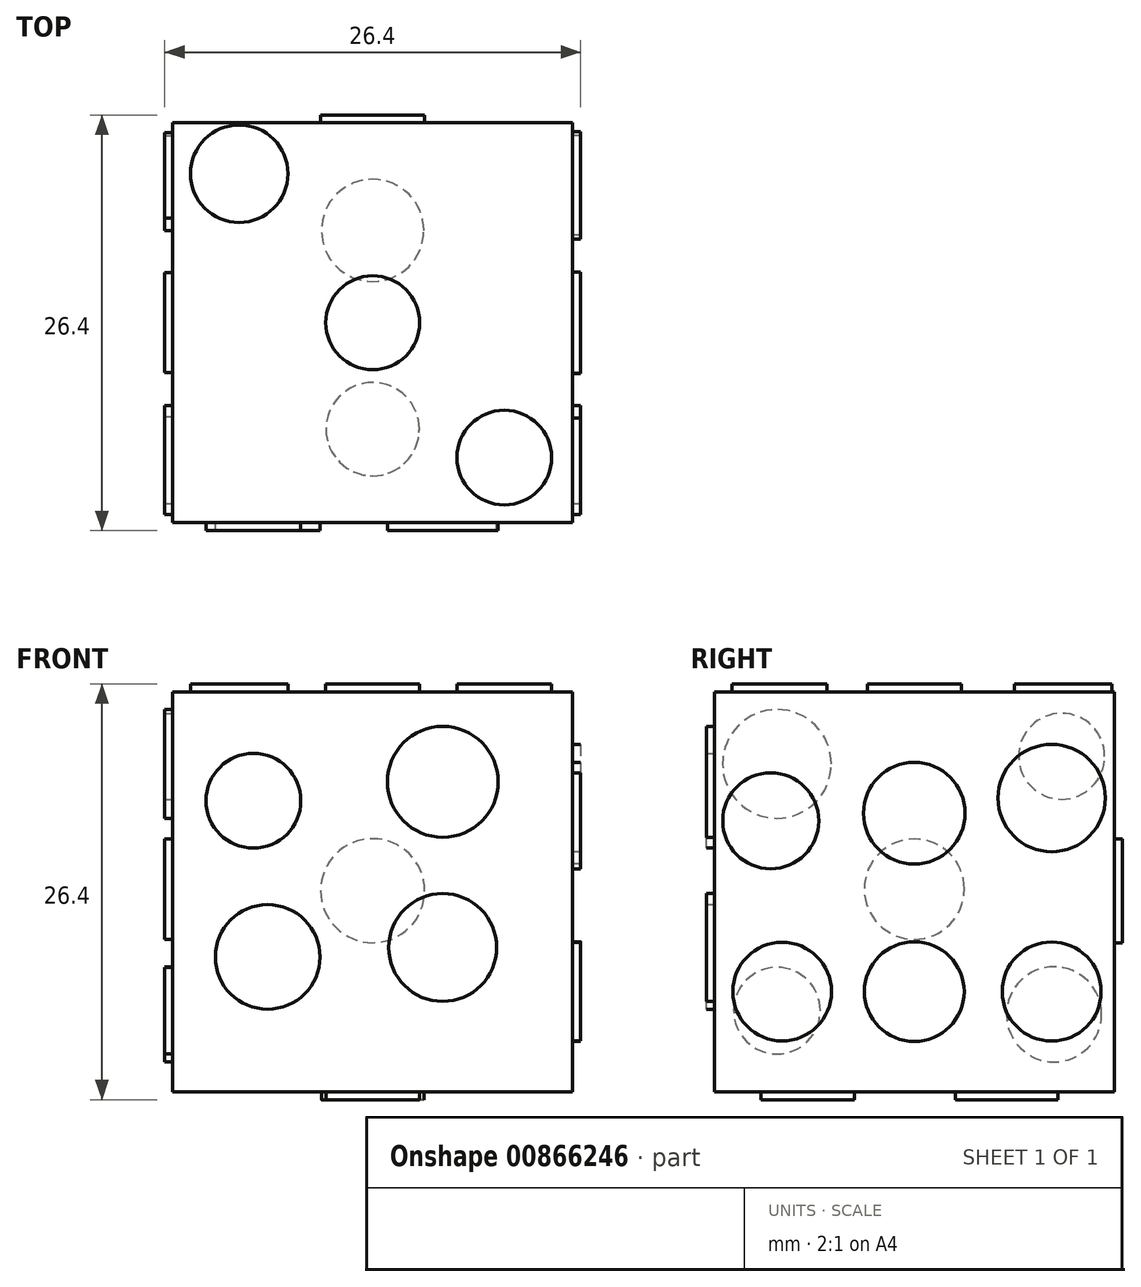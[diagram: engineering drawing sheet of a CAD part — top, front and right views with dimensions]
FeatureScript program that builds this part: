
annotation { "Feature Type Name" : "Feature", "Feature Type Description" : "" }
export const myFeature = defineFeature(function(context is Context, id is Id, definition is map)
    precondition{}
    {
        {
            var Q0;
            Q0=qCreatedBy(makeId("Top.planeOp"),FACE);
            var sketch = newSketch(context, id + "F0", { "sketchPlane" : qUnion([Q0])});
            skLineSegment(sketch, "E0.bottom", {"start": v(12.7, -12.7) * mm, "end": v(-12.7, -12.7) * mm});
            skLineSegment(sketch, "E0.top", {"start": v(12.7, 12.7) * mm, "end": v(-12.7, 12.7) * mm});
            skLineSegment(sketch, "E0.left", {"start": v(12.7, -12.7) * mm, "end": v(12.7, 12.7) * mm});
            skLineSegment(sketch, "E0.right", {"start": v(-12.7, -12.7) * mm, "end": v(-12.7, 12.7) * mm});
            skPoint(sketch, "E0.middle", {"position": v(0, 0) * mm});
            skSolve(sketch);
        }
        {
            var Q0;
            Q0 = qSketchRegion(id + "F0", true);
            extrude(context, id + "F1", {"entities" : qUnion([Q0]), "depth" : 25.4 * mm, "offsetDistance" : 25 * mm});
        }
        {
            var Q0;
            Q0=makeQuery(id+"F1.opExtrude","SWEPT_FACE",FACE,{"disambiguationData":[OSD([sQuery(id+"F0.wireOp",EDGE,"E0.top")])]});
            var sketch = newSketch(context, id + "F2", { "sketchPlane" : qUnion([Q0])});
            skCircle(sketch, "E1", {"center": v(0, 12.77) * mm, "radius": 3.3 * mm});
            skSolve(sketch);
        }
        {
            var Q0;
            Q0 = qSketchRegion(id + "F2", true);
            extrude(context, id + "F3", {"entities" : qUnion([Q0]), "operationType" : NewBodyOperationType.ADD, "depth" : .5 * mm, "offsetDistance" : 25 * mm});
        }
        {
            var Q0;
            Q0=makeQuery(id+"F1.opExtrude","CAP_FACE",FACE,{"disambiguationData":[OSD([sQuery(id+"F0.wireOp",EDGE,"E0.bottom"),sQuery(id+"F0.wireOp",EDGE,"E0.top"),sQuery(id+"F0.wireOp",EDGE,"E0.left"),sQuery(id+"F0.wireOp",EDGE,"E0.right")])],"isStart":true});
            var sketch = newSketch(context, id + "F4", { "sketchPlane" : qUnion([Q0])});
            skCircle(sketch, "E2", {"center": v(0, -5.86) * mm, "radius": 3.25 * mm});
            skCircle(sketch, "E3", {"center": v(0, 6.76) * mm, "radius": 2.96 * mm});
            skSolve(sketch);
        }
        {
            var Q0;
            Q0 = qSketchRegion(id + "F4", true);
            extrude(context, id + "F5", {"entities" : qUnion([Q0]), "operationType" : NewBodyOperationType.ADD, "depth" : .5 * mm, "offsetDistance" : 25 * mm});
        }
        {
            var Q0;
            Q0=makeQuery(id+"F1.opExtrude","CAP_FACE",FACE,{"disambiguationData":[OSD([sQuery(id+"F0.wireOp",EDGE,"E0.bottom"),sQuery(id+"F0.wireOp",EDGE,"E0.top"),sQuery(id+"F0.wireOp",EDGE,"E0.left"),sQuery(id+"F0.wireOp",EDGE,"E0.right")])],"isStart":false});
            var sketch = newSketch(context, id + "F6", { "sketchPlane" : qUnion([Q0])});
            skCircle(sketch, "E4", {"center": v(8.36, -8.57) * mm, "radius": 3 * mm});
            skCircle(sketch, "E5", {"center": v(0, 0) * mm, "radius": 2.98 * mm});
            skCircle(sketch, "E6", {"center": v(-8.48, 9.47) * mm, "radius": 3.1 * mm});
            skSolve(sketch);
        }
        {
            var Q0;
            Q0 = qSketchRegion(id + "F6", true);
            extrude(context, id + "F7", {"entities" : qUnion([Q0]), "operationType" : NewBodyOperationType.ADD, "depth" : .5 * mm, "offsetDistance" : 25 * mm});
        }
        {
            var Q0;
            Q0=makeQuery(id+"F1.opExtrude","SWEPT_FACE",FACE,{"disambiguationData":[OSD([sQuery(id+"F0.wireOp",EDGE,"E0.bottom")])]});
            var sketch = newSketch(context, id + "F8", { "sketchPlane" : qUnion([Q0])});
            skCircle(sketch, "E7", {"center": v(-6.67, 8.57) * mm, "radius": 3.32 * mm});
            skCircle(sketch, "E8", {"center": v(4.45, 9.17) * mm, "radius": 3.43 * mm});
            skCircle(sketch, "E9", {"center": v(-7.57, 18.49) * mm, "radius": 3 * mm});
            skCircle(sketch, "E10", {"center": v(4.45, 19.69) * mm, "radius": 3.52 * mm});
            skSolve(sketch);
        }
        {
            var Q0;
            Q0 = qSketchRegion(id + "F8", true);
            extrude(context, id + "F9", {"entities" : qUnion([Q0]), "operationType" : NewBodyOperationType.ADD, "depth" : .5 * mm, "offsetDistance" : 25 * mm});
        }
        {
            var Q0;
            Q0=makeQuery(id+"F1.opExtrude","SWEPT_FACE",FACE,{"disambiguationData":[OSD([sQuery(id+"F0.wireOp",EDGE,"E0.right")])]});
            var sketch = newSketch(context, id + "F10", { "sketchPlane" : qUnion([Q0])});
            skCircle(sketch, "E11", {"center": v(-8.88, 4.92) * mm, "radius": 3.02 * mm});
            skCircle(sketch, "E12", {"center": v(0, 12.87) * mm, "radius": 3.18 * mm});
            skCircle(sketch, "E13", {"center": v(-9.36, 21.31) * mm, "radius": 2.73 * mm});
            skCircle(sketch, "E14", {"center": v(8.72, 20.83) * mm, "radius": 3.45 * mm});
            skCircle(sketch, "E15", {"center": v(8.72, 5.16) * mm, "radius": 2.75 * mm});
            skSolve(sketch);
        }
        {
            var Q0;
            Q0 = qSketchRegion(id + "F10", true);
            extrude(context, id + "F11", {"entities" : qUnion([Q0]), "operationType" : NewBodyOperationType.ADD, "depth" : .5 * mm, "offsetDistance" : 25 * mm});
        }
        {
            var Q0;
            Q0=makeQuery(id+"F1.opExtrude","SWEPT_FACE",FACE,{"disambiguationData":[OSD([sQuery(id+"F0.wireOp",EDGE,"E0.left")])]});
            var sketch = newSketch(context, id + "F12", { "sketchPlane" : qUnion([Q0])});
            skCircle(sketch, "E16", {"center": v(-8.4, 6.36) * mm, "radius": 3.13 * mm});
            skCircle(sketch, "E17", {"center": v(0, 6.36) * mm, "radius": 3.17 * mm});
            skCircle(sketch, "E18", {"center": v(8.72, 6.36) * mm, "radius": 3.14 * mm});
            skCircle(sketch, "E19", {"center": v(-9.12, 17.21) * mm, "radius": 3.05 * mm});
            skCircle(sketch, "E20", {"center": v(0, 17.7) * mm, "radius": 3.23 * mm});
            skCircle(sketch, "E21", {"center": v(8.72, 18.66) * mm, "radius": 3.4 * mm});
            skSolve(sketch);
        }
        {
            var Q0;
            Q0 = qSketchRegion(id + "F12", true);
            extrude(context, id + "F13", {"entities" : qUnion([Q0]), "operationType" : NewBodyOperationType.ADD, "depth" : .5 * mm, "offsetDistance" : 25 * mm});
        }
    });
